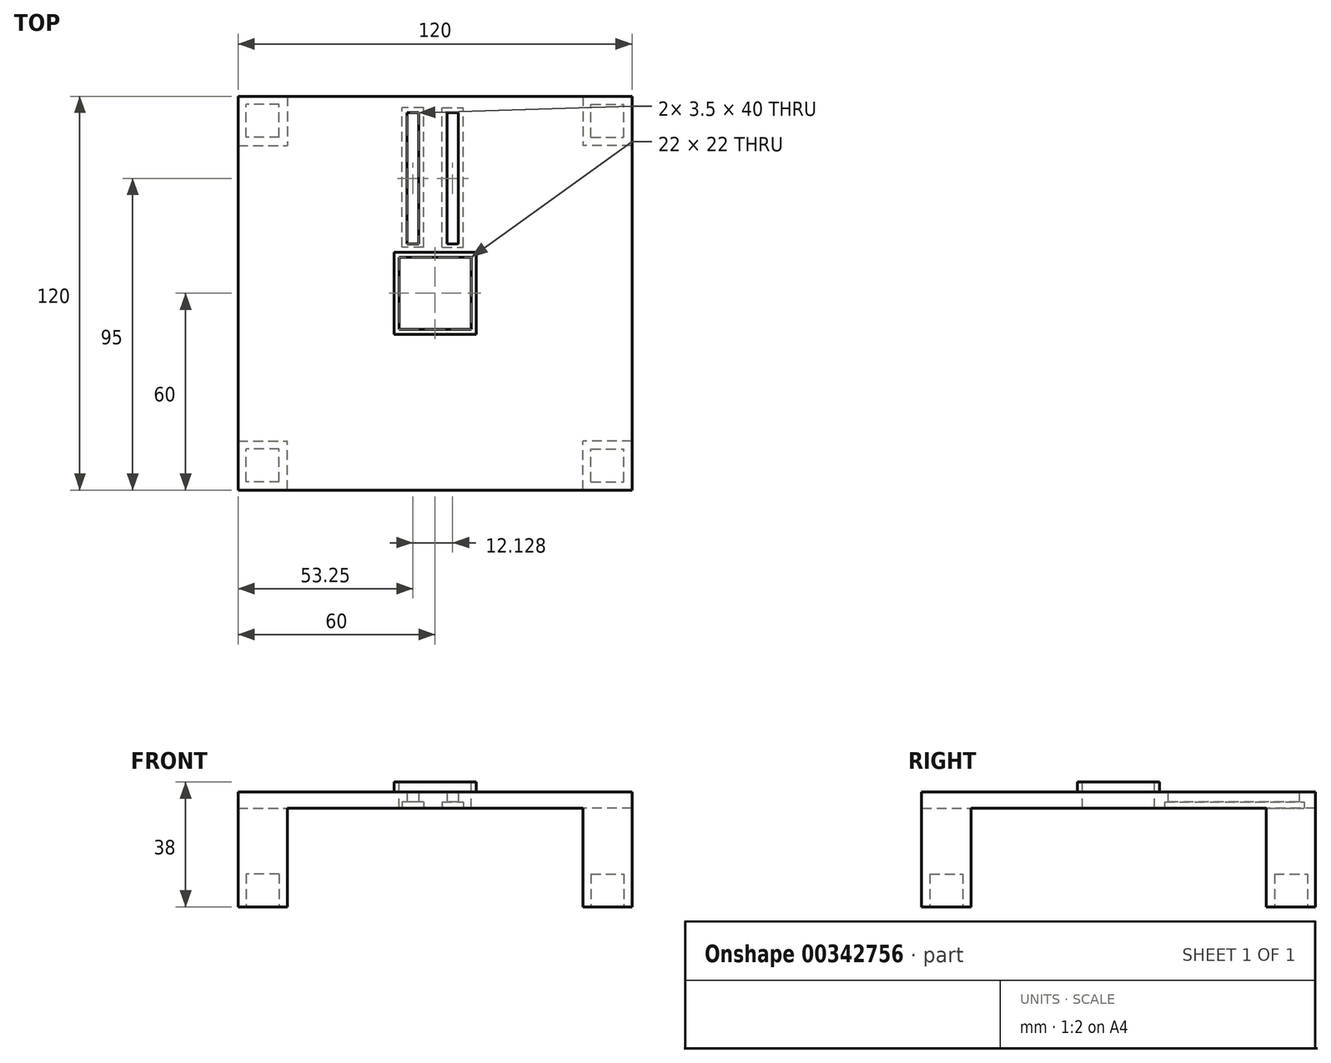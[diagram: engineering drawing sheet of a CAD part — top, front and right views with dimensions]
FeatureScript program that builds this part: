
annotation { "Feature Type Name" : "Feature", "Feature Type Description" : "" }
export const myFeature = defineFeature(function(context is Context, id is Id, definition is map)
    precondition{}
    {
        {
            var Q0;
            Q0=qCreatedBy(makeId("Top.planeOp"),FACE);
            var sketch = newSketch(context, id + "F0", { "sketchPlane" : qUnion([Q0])});
            skLineSegment(sketch, "E0.bottom", {"start": v(60, 60) * mm, "end": v(-60, 60) * mm});
            skLineSegment(sketch, "E0.top", {"start": v(60, -60) * mm, "end": v(-60, -60) * mm});
            skLineSegment(sketch, "E0.left", {"start": v(60, 60) * mm, "end": v(60, -60) * mm});
            skLineSegment(sketch, "E0.right", {"start": v(-60, 60) * mm, "end": v(-60, -60) * mm});
            skPoint(sketch, "E0.middle", {"position": v(0, 0) * mm});
            skSolve(sketch);
        }
        {
            var Q0;
            Q0 = qSketchRegion(id + "F0", true);
            extrude(context, id + "F1", {"entities" : qUnion([Q0]), "oppositeDirection" : true, "depth" : 5 * mm});
        }
        {
            var Q0;
            Q0=makeQuery(id+"F1.opExtrude","CAP_FACE",FACE,{"disambiguationData":[OSD([sQuery(id+"F0.wireOp",EDGE,"E0.bottom"),sQuery(id+"F0.wireOp",EDGE,"E0.top"),sQuery(id+"F0.wireOp",EDGE,"E0.left"),sQuery(id+"F0.wireOp",EDGE,"E0.right")])],"isStart":false});
            var sketch = newSketch(context, id + "F2", { "sketchPlane" : qUnion([Q0])});
            skLineSegment(sketch, "E1.bottom", {"start": v(-60, 60) * mm, "end": v(-45, 60) * mm});
            skLineSegment(sketch, "E1.top", {"start": v(-60, 45) * mm, "end": v(-45, 45) * mm});
            skLineSegment(sketch, "E1.left", {"start": v(-60, 60) * mm, "end": v(-60, 45) * mm});
            skLineSegment(sketch, "E1.right", {"start": v(-45, 60) * mm, "end": v(-45, 45) * mm});
            skLineSegment(sketch, "E2.bottom", {"start": v(-60, -60) * mm, "end": v(-45, -60) * mm});
            skLineSegment(sketch, "E2.top", {"start": v(-60, -45) * mm, "end": v(-45, -45) * mm});
            skLineSegment(sketch, "E2.left", {"start": v(-60, -60) * mm, "end": v(-60, -45) * mm});
            skLineSegment(sketch, "E2.right", {"start": v(-45, -60) * mm, "end": v(-45, -45) * mm});
            skLineSegment(sketch, "E3.bottom", {"start": v(60, -60) * mm, "end": v(45, -60) * mm});
            skLineSegment(sketch, "E3.top", {"start": v(60, -45) * mm, "end": v(45, -45) * mm});
            skLineSegment(sketch, "E3.left", {"start": v(60, -60) * mm, "end": v(60, -45) * mm});
            skLineSegment(sketch, "E3.right", {"start": v(45, -60) * mm, "end": v(45, -45) * mm});
            skLineSegment(sketch, "E4.bottom", {"start": v(60, 60) * mm, "end": v(45, 60) * mm});
            skLineSegment(sketch, "E4.top", {"start": v(60, 45) * mm, "end": v(45, 45) * mm});
            skLineSegment(sketch, "E4.left", {"start": v(60, 60) * mm, "end": v(60, 45) * mm});
            skLineSegment(sketch, "E4.right", {"start": v(45, 60) * mm, "end": v(45, 45) * mm});
            skSolve(sketch);
        }
        {
            var Q0;
            Q0 = qSketchRegion(id + "F2", true);
            extrude(context, id + "F3", {"entities" : qUnion([Q0]), "operationType" : NewBodyOperationType.ADD, "depth" : 30 * mm});
        }
        {
            var Q0;
            Q0=makeQuery(id+"F3.opExtrude","CAP_FACE",FACE,{"disambiguationData":[OSD([sQuery(id+"F2.wireOp",EDGE,"E1.bottom"),sQuery(id+"F2.wireOp",EDGE,"E1.top"),sQuery(id+"F2.wireOp",EDGE,"E1.left"),sQuery(id+"F2.wireOp",EDGE,"E1.right")])],"isStart":false});
            var sketch = newSketch(context, id + "F4", { "sketchPlane" : qUnion([Q0])});
            skLineSegment(sketch, "E5.bottom", {"start": v(-47.5, 57.5) * mm, "end": v(-57.5, 57.5) * mm});
            skLineSegment(sketch, "E5.top", {"start": v(-47.5, 47.5) * mm, "end": v(-57.5, 47.5) * mm});
            skLineSegment(sketch, "E5.left", {"start": v(-47.5, 57.5) * mm, "end": v(-47.5, 47.5) * mm});
            skLineSegment(sketch, "E5.right", {"start": v(-57.5, 57.5) * mm, "end": v(-57.5, 47.5) * mm});
            skPoint(sketch, "E5.middle", {"position": v(-52.5, 52.5) * mm});
            skPoint(sketch, "E5.middle.positionSnap0", {"position": v(-60, 52.5) * mm});
            skPoint(sketch, "E5.middle.positionSnap1", {"position": v(-52.5, 45) * mm});
            skPoint(sketch, "E5.centerSnap0", {"position": v(-60, 52.5) * mm});
            skPoint(sketch, "E5.centerSnap1", {"position": v(-52.5, 45) * mm});
            skLineSegment(sketch, "E6.bottom", {"start": v(-47.5, -47.5) * mm, "end": v(-57.5, -47.5) * mm});
            skLineSegment(sketch, "E6.top", {"start": v(-47.5, -57.5) * mm, "end": v(-57.5, -57.5) * mm});
            skLineSegment(sketch, "E6.left", {"start": v(-47.5, -47.5) * mm, "end": v(-47.5, -57.5) * mm});
            skLineSegment(sketch, "E6.right", {"start": v(-57.5, -47.5) * mm, "end": v(-57.5, -57.5) * mm});
            skLineSegment(sketch, "E7.bottom", {"start": v(47.5, -47.5) * mm, "end": v(57.5, -47.5) * mm});
            skLineSegment(sketch, "E7.top", {"start": v(47.5, -57.5) * mm, "end": v(57.5, -57.5) * mm});
            skLineSegment(sketch, "E7.left", {"start": v(47.5, -47.5) * mm, "end": v(47.5, -57.5) * mm});
            skLineSegment(sketch, "E7.right", {"start": v(57.5, -47.5) * mm, "end": v(57.5, -57.5) * mm});
            skPoint(sketch, "E7.middle", {"position": v(52.5, -52.5) * mm});
            skPoint(sketch, "E7.middle.positionSnap0", {"position": v(-47.5, -52.5) * mm});
            skPoint(sketch, "E7.centerSnap0", {"position": v(-47.5, -52.5) * mm});
            skLineSegment(sketch, "E8.bottom", {"start": v(47.5, 57.5) * mm, "end": v(57.5, 57.5) * mm});
            skLineSegment(sketch, "E8.top", {"start": v(47.5, 47.5) * mm, "end": v(57.5, 47.5) * mm});
            skLineSegment(sketch, "E8.left", {"start": v(47.5, 57.5) * mm, "end": v(47.5, 47.5) * mm});
            skLineSegment(sketch, "E8.right", {"start": v(57.5, 57.5) * mm, "end": v(57.5, 47.5) * mm});
            skPoint(sketch, "E8.middle", {"position": v(52.5, 52.5) * mm});
            skSolve(sketch);
        }
        {
            var Q0;
            Q0 = qSketchRegion(id + "F4", true);
            extrude(context, id + "F5", {"entities" : qUnion([Q0]), "operationType" : NewBodyOperationType.REMOVE, "oppositeDirection" : true, "depth" : 10 * mm});
        }
        {
            var Q0;
            Q0=makeQuery(id+"F1.opExtrude","CAP_FACE",FACE,{"disambiguationData":[OSD([sQuery(id+"F0.wireOp",EDGE,"E0.bottom"),sQuery(id+"F0.wireOp",EDGE,"E0.top"),sQuery(id+"F0.wireOp",EDGE,"E0.left"),sQuery(id+"F0.wireOp",EDGE,"E0.right")])],"isStart":true});
            var sketch = newSketch(context, id + "F6", { "sketchPlane" : qUnion([Q0])});
            skLineSegment(sketch, "E9.bottom", {"start": v(12.5, 12.5) * mm, "end": v(-12.5, 12.5) * mm});
            skLineSegment(sketch, "E9.top", {"start": v(12.5, -12.5) * mm, "end": v(-12.5, -12.5) * mm});
            skLineSegment(sketch, "E9.left", {"start": v(12.5, 12.5) * mm, "end": v(12.5, -12.5) * mm});
            skLineSegment(sketch, "E9.right", {"start": v(-12.5, 12.5) * mm, "end": v(-12.5, -12.5) * mm});
            skPoint(sketch, "E9.middle", {"position": v(0, 0) * mm});
            skSolve(sketch);
        }
        {
            var Q0;
            Q0 = qSketchRegion(id + "F6", true);
            extrude(context, id + "F7", {"entities" : qUnion([Q0]), "operationType" : NewBodyOperationType.ADD, "depth" : 3 * mm});
        }
        {
            var Q0;
            Q0=makeQuery(id+"F7.opExtrude","CAP_FACE",FACE,{"disambiguationData":[OSD([sQuery(id+"F6.wireOp",EDGE,"E9.bottom"),sQuery(id+"F6.wireOp",EDGE,"E9.top"),sQuery(id+"F6.wireOp",EDGE,"E9.left"),sQuery(id+"F6.wireOp",EDGE,"E9.right")])],"isStart":false});
            var sketch = newSketch(context, id + "F8", { "sketchPlane" : qUnion([Q0])});
            skLineSegment(sketch, "E10.bottom", {"start": v(11, 11) * mm, "end": v(-11, 11) * mm});
            skLineSegment(sketch, "E10.top", {"start": v(11, -11) * mm, "end": v(-11, -11) * mm});
            skLineSegment(sketch, "E10.left", {"start": v(11, 11) * mm, "end": v(11, -11) * mm});
            skLineSegment(sketch, "E10.right", {"start": v(-11, 11) * mm, "end": v(-11, -11) * mm});
            skPoint(sketch, "E10.middle", {"position": v(0, 0) * mm});
            skSolve(sketch);
        }
        {
            var Q0;
            Q0 = qSketchRegion(id + "F8", true);
            extrude(context, id + "F9", {"entities" : qUnion([Q0]), "operationType" : NewBodyOperationType.REMOVE, "endBound" : BoundingType.UP_TO_NEXT, "oppositeDirection" : true, "depth" : 15 * mm});
        }
        {
            var Q0;
            Q0=makeQuery(id+"F1.opExtrude","CAP_FACE",FACE,{"disambiguationData":[OSD([sQuery(id+"F0.wireOp",EDGE,"E0.bottom"),sQuery(id+"F0.wireOp",EDGE,"E0.top"),sQuery(id+"F0.wireOp",EDGE,"E0.left"),sQuery(id+"F0.wireOp",EDGE,"E0.right")])],"isStart":false});
            var sketch = newSketch(context, id + "F10", { "sketchPlane" : qUnion([Q0])});
            skLineSegment(sketch, "E11.bottom", {"start": v(-8.5, -15) * mm, "end": v(-5, -15) * mm});
            skLineSegment(sketch, "E11.top", {"start": v(-8.5, -55) * mm, "end": v(-5, -55) * mm});
            skLineSegment(sketch, "E11.left", {"start": v(-8.5, -15) * mm, "end": v(-8.5, -55) * mm});
            skLineSegment(sketch, "E11.right", {"start": v(-5, -15) * mm, "end": v(-5, -55) * mm});
            skLineSegment(sketch, "E12.bottom", {"start": v(3.63, -15) * mm, "end": v(7.13, -15) * mm});
            skLineSegment(sketch, "E12.top", {"start": v(3.63, -55) * mm, "end": v(7.13, -55) * mm});
            skLineSegment(sketch, "E12.left", {"start": v(3.63, -15) * mm, "end": v(3.63, -55) * mm});
            skLineSegment(sketch, "E12.right", {"start": v(7.13, -15) * mm, "end": v(7.13, -55) * mm});
            skSolve(sketch);
        }
        {
            var Q0;
            Q0 = qSketchRegion(id + "F10", true);
            extrude(context, id + "F11", {"entities" : qUnion([Q0]), "operationType" : NewBodyOperationType.REMOVE, "endBound" : BoundingType.UP_TO_NEXT, "oppositeDirection" : true, "depth" : 25 * mm});
        }
        {
            var Q0;
            Q0=qCreatedBy(makeId("Front.planeOp"),FACE);
            var sketch = newSketch(context, id + "F12", { "sketchPlane" : qUnion([Q0])});
            skLineSegment(sketch, "E13", {"start": v(0, 0) * mm, "end": v(0, 17.05) * mm});
            skSolve(sketch);
        }
        {
            var Q0;
            Q0=makeQuery(id+"F1.opExtrude","CAP_FACE",FACE,{"disambiguationData":[OSD([sQuery(id+"F0.wireOp",EDGE,"E0.bottom"),sQuery(id+"F0.wireOp",EDGE,"E0.top"),sQuery(id+"F0.wireOp",EDGE,"E0.left"),sQuery(id+"F0.wireOp",EDGE,"E0.right")])],"isStart":false});
            var sketch = newSketch(context, id + "F13", { "sketchPlane" : qUnion([Q0])});
            skLineSegment(sketch, "E14.bottom", {"start": v(2.13, -14) * mm, "end": v(8.63, -14) * mm});
            skLineSegment(sketch, "E14.top", {"start": v(2.13, -56.5) * mm, "end": v(8.63, -56.5) * mm});
            skLineSegment(sketch, "E14.left", {"start": v(2.13, -14) * mm, "end": v(2.13, -56.5) * mm});
            skLineSegment(sketch, "E14.right", {"start": v(8.63, -14) * mm, "end": v(8.63, -56.5) * mm});
            skLineSegment(sketch, "E15.bottom", {"start": v(-3.5, -14) * mm, "end": v(-10, -14) * mm});
            skLineSegment(sketch, "E15.top", {"start": v(-3.5, -56.5) * mm, "end": v(-10, -56.5) * mm});
            skLineSegment(sketch, "E15.left", {"start": v(-3.5, -14) * mm, "end": v(-3.5, -56.5) * mm});
            skLineSegment(sketch, "E15.right", {"start": v(-10, -14) * mm, "end": v(-10, -56.5) * mm});
            skSolve(sketch);
        }
        {
            var Q0;
            Q0 = qSketchRegion(id + "F13", true);
            extrude(context, id + "F14", {"entities" : qUnion([Q0]), "operationType" : NewBodyOperationType.REMOVE, "oppositeDirection" : true, "depth" : 2 * mm});
        }
        {
            var Q0;
            Q0=qCreatedBy(makeId("Front.planeOp"),FACE);
            var sketch = newSketch(context, id + "F15", { "sketchPlane" : qUnion([Q0])});
            skLineSegment(sketch, "E16", {"start": v(0, 0) * mm, "end": v(0, 28.61) * mm, "construction": true});
            skSolve(sketch);
        }
    });
